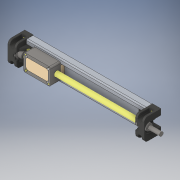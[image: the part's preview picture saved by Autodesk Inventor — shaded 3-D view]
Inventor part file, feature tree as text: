
AUTODESK INVENTOR PART (.ipt)
format: ipt  version: 2019 (Build 230136000, 136)  size: 593,408 bytes
history: native  units: mm
features: other x4, extrude x1, sketch x1
ambient origin geometry x8: Origin, YZ Plane, XZ Plane, XY Plane, X Axis, Y Axis, Z Axis, Center Point
bodies: Solid1 (feature_tree), Solid2 (feature_tree)
feature tree (6):
  other  "SLNV_27_100_2_MIR.ipt"
  extrude  "Extrusion1"  Depth=10.0mm
  other  "Solid1::SLNV_27_100_2_MIR.ipt"
  other  "Solid2::SLNV_27_100_2_MIR.ipt"
  other  "TaggingFeature1"
  sketch  "Sketch1"  dims[d0=10.0mm d1=28.0mm d2=15.0mm d3=3.0mm d4=3.0mm d5=3.0mm d6=3.0mm d7=10.0mm d8=0.0mm]
